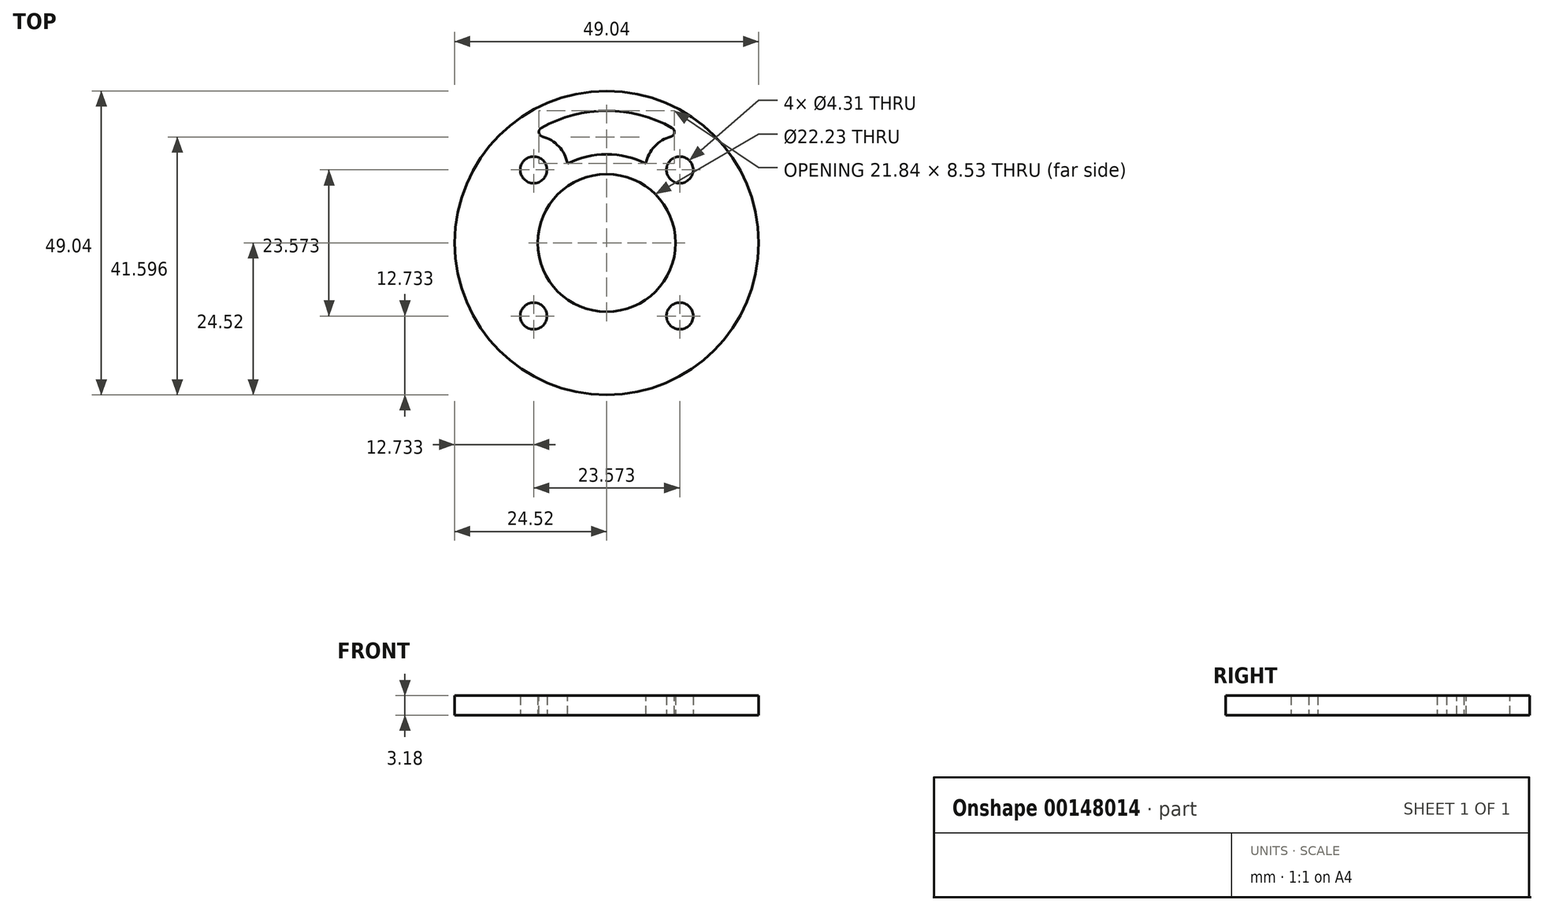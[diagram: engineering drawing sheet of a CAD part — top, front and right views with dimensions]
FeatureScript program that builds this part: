
annotation { "Feature Type Name" : "Feature", "Feature Type Description" : "" }
export const myFeature = defineFeature(function(context is Context, id is Id, definition is map)
    precondition{}
    {
        {
            var Q0;
            Q0=qCreatedBy(makeId("Top.planeOp"),FACE);
            var sketch = newSketch(context, id + "F0", { "sketchPlane" : qUnion([Q0])});
            skCircle(sketch, "E0", {"center": v(0, 0) * mm, "radius": 24.52 * mm});
            skCircle(sketch, "E1", {"center": v(0, 0) * mm, "radius": 11.11 * mm});
            skLineSegment(sketch, "E2.bottom", {"start": v(-11.79, 11.79) * mm, "end": v(11.79, 11.79) * mm, "construction": true});
            skLineSegment(sketch, "E2.top", {"start": v(-11.79, -11.79) * mm, "end": v(11.79, -11.79) * mm, "construction": true});
            skLineSegment(sketch, "E2.left", {"start": v(-11.79, 11.79) * mm, "end": v(-11.79, -11.79) * mm, "construction": true});
            skLineSegment(sketch, "E2.right", {"start": v(11.79, 11.79) * mm, "end": v(11.79, -11.79) * mm, "construction": true});
            skCircle(sketch, "E3", {"center": v(-11.79, 11.79) * mm, "radius": 5.56 * mm, "construction": true});
            skCircle(sketch, "E4", {"center": v(11.79, 11.79) * mm, "radius": 2.15 * mm});
            skCircle(sketch, "E5", {"center": v(-11.79, 11.79) * mm, "radius": 2.15 * mm});
            skCircle(sketch, "E6", {"center": v(-11.79, -11.79) * mm, "radius": 2.15 * mm});
            skCircle(sketch, "E7", {"center": v(11.79, -11.79) * mm, "radius": 2.15 * mm});
            skCircle(sketch, "E8", {"center": v(-11.79, -11.79) * mm, "radius": 3.97 * mm, "construction": true});
            skCircle(sketch, "E9", {"center": v(11.79, 11.79) * mm, "radius": 3.97 * mm, "construction": true});
            skSolve(sketch);
        }
        {
            var Q0;
            Q0=qSketchRegion(id+"F0",true);
            extrude(context, id + "F1", {"entities" : qUnion([Q0]), "depth" : 3.17 * mm});
        }
        {
            var Q0;
            Q0=makeQuery(id+"F1.opExtrude","CAP_FACE",FACE,{"disambiguationData":[OSD([sQuery(id+"F0.wireOp",EDGE,"E0"),sQuery(id+"F0.wireOp",EDGE,"E1"),sQuery(id+"F0.wireOp",EDGE,"E4"),sQuery(id+"F0.wireOp",EDGE,"E5"),sQuery(id+"F0.wireOp",EDGE,"E6"),sQuery(id+"F0.wireOp",EDGE,"E7")])],"isStart":false});
            var sketch = newSketch(context, id + "F2", { "sketchPlane" : qUnion([Q0])});
            skArc(sketch, "E10", {"start": v(-6.33, 12.81) * mm, "mid": v(-8.52, 16.28) * mm, "end": v(-12.5, 17.3) * mm});
            skArc(sketch, "E11", {"start": v(12.5, 17.3) * mm, "mid": v(8.52, 16.28) * mm, "end": v(6.33, 12.81) * mm});
            skArc(sketch, "E12", {"start": v(12.5, 17.3) * mm, "mid": v(0, 21.34) * mm, "end": v(-12.5, 17.3) * mm});
            skArc(sketch, "E13", {"start": v(6.33, 12.81) * mm, "mid": v(0, 14.29) * mm, "end": v(-6.33, 12.81) * mm});
            skSolve(sketch);
        }
        {
            var Q0;
            Q0=makeQuery(id+"F2.imprint","IMPRINT",FACE,{"disambiguationData":[TD([[makeQuery(id+"F2.imprint","IMPRINT",EDGE,{"derivedFrom":sQuery(id+"F2.wireOp",EDGE,"E10")}),-1.0]])]});
            var Q1;
            Q1=makeQuery(id+"F1.opExtrude","CAP_FACE",FACE,{"disambiguationData":[OSD([sQuery(id+"F0.wireOp",EDGE,"E0"),sQuery(id+"F0.wireOp",EDGE,"E1"),sQuery(id+"F0.wireOp",EDGE,"E4"),sQuery(id+"F0.wireOp",EDGE,"E5"),sQuery(id+"F0.wireOp",EDGE,"E6"),sQuery(id+"F0.wireOp",EDGE,"E7")])],"isStart":true});
            extrude(context, id + "F3", {"entities" : qUnion([Q0]), "operationType" : NewBodyOperationType.REMOVE, "endBound" : BoundingType.UP_TO_SURFACE, "oppositeDirection" : true, "endBoundEntityFace" : qUnion([Q1]), "depth" : 25.4 * mm});
        }
        {
            var Q0;
            Q0=makeQuery(id+"F6MqURjXbY15YYN_1.1.F3.boolean.opBoolean","COPY",EDGE,{"derivedFrom":makeQuery(id+"F6MqURjXbY15YYN_1.1.F3.opExtrude","SWEPT_EDGE",EDGE,{"disambiguationData":[OSD([sQuery(id+"F2.wireOp",EDGE,"E10"),sQuery(id+"F2.wireOp",EDGE,"E12")])]})});
            var Q1;
            Q1=makeQuery(id+"F6MqURjXbY15YYN_1.1.F3.boolean.opBoolean","COPY",EDGE,{"derivedFrom":makeQuery(id+"F6MqURjXbY15YYN_1.1.F3.opExtrude","SWEPT_EDGE",EDGE,{"disambiguationData":[OSD([sQuery(id+"F2.wireOp",EDGE,"E11"),sQuery(id+"F2.wireOp",EDGE,"E12")])]})});
            var Q2;
            Q2=makeQuery(id+"F6MqURjXbY15YYN_1.2.F3.boolean.opBoolean","COPY",EDGE,{"derivedFrom":makeQuery(id+"F6MqURjXbY15YYN_1.2.F3.opExtrude","SWEPT_EDGE",EDGE,{"disambiguationData":[OSD([sQuery(id+"F2.wireOp",EDGE,"E10"),sQuery(id+"F2.wireOp",EDGE,"E12")])]})});
            var Q3;
            Q3=makeQuery(id+"F6MqURjXbY15YYN_1.2.F3.boolean.opBoolean","COPY",EDGE,{"derivedFrom":makeQuery(id+"F6MqURjXbY15YYN_1.2.F3.opExtrude","SWEPT_EDGE",EDGE,{"disambiguationData":[OSD([sQuery(id+"F2.wireOp",EDGE,"E11"),sQuery(id+"F2.wireOp",EDGE,"E12")])]})});
            var Q4;
            Q4=makeQuery(id+"F6MqURjXbY15YYN_1.3.F3.boolean.opBoolean","COPY",EDGE,{"derivedFrom":makeQuery(id+"F6MqURjXbY15YYN_1.3.F3.opExtrude","SWEPT_EDGE",EDGE,{"disambiguationData":[OSD([sQuery(id+"F2.wireOp",EDGE,"E10"),sQuery(id+"F2.wireOp",EDGE,"E12")])]})});
            var Q5;
            Q5=makeQuery(id+"F6MqURjXbY15YYN_1.3.F3.boolean.opBoolean","COPY",EDGE,{"derivedFrom":makeQuery(id+"F6MqURjXbY15YYN_1.3.F3.opExtrude","SWEPT_EDGE",EDGE,{"disambiguationData":[OSD([sQuery(id+"F2.wireOp",EDGE,"E11"),sQuery(id+"F2.wireOp",EDGE,"E12")])]})});
            var Q6;
            Q6=makeQuery(id+"F3.boolean.opBoolean","COPY",EDGE,{"derivedFrom":makeQuery(id+"F3.opExtrude","SWEPT_EDGE",EDGE,{"disambiguationData":[OSD([sQuery(id+"F2.wireOp",EDGE,"E10"),sQuery(id+"F2.wireOp",EDGE,"E12")])]})});
            var Q7;
            Q7=makeQuery(id+"F3.boolean.opBoolean","COPY",EDGE,{"derivedFrom":makeQuery(id+"F3.opExtrude","SWEPT_EDGE",EDGE,{"disambiguationData":[OSD([sQuery(id+"F2.wireOp",EDGE,"E11"),sQuery(id+"F2.wireOp",EDGE,"E12")])]})});
            fillet(context, id + "F4", {"entities" : qUnion([Q0, Q1, Q2, Q3, Q4, Q5, Q6, Q7]), "radius" : 0.76 * mm, "tangentPropagation" : true, "allowEdgeOverflow" : false});
        }
    });
